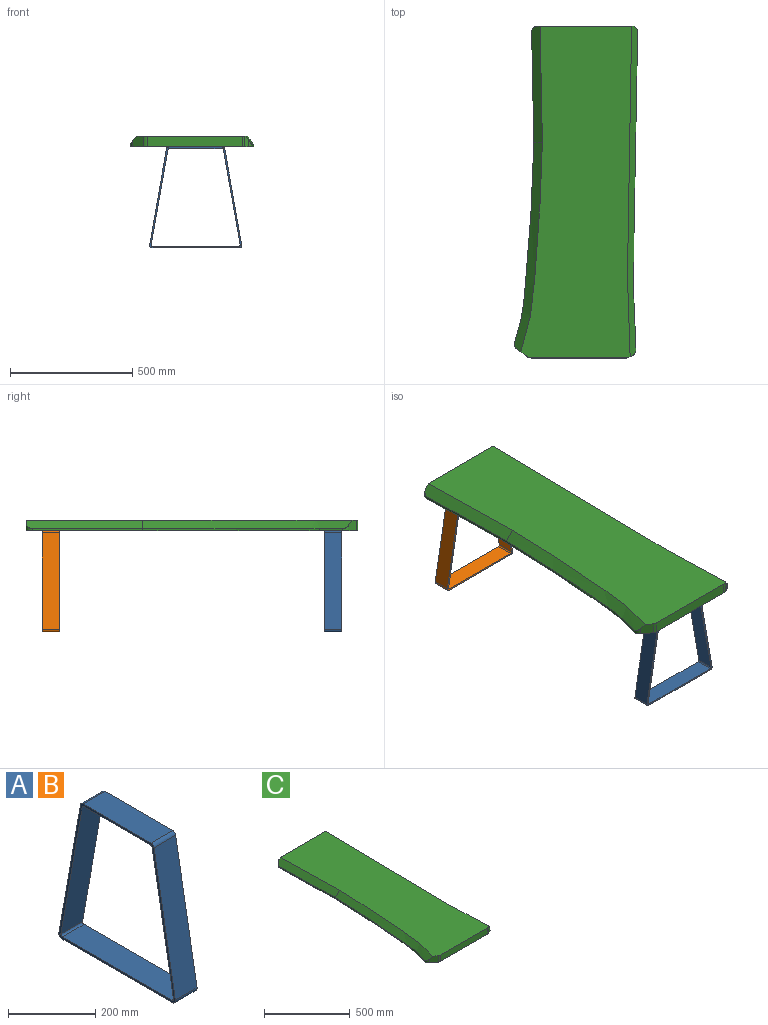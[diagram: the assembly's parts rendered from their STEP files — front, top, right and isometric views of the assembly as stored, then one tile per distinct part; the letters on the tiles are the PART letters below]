
ASSEMBLY  parts=3 mates=2
PART A: 18 faces, bbox 70x377.2x412.8 mm
  f0: plane 412.75x377.17mm, normal (1,0,0), area 9004.4mm2, adj f2,f3,f4,f5,f6,f7,f8,f9
  f1: plane 412.75x377.17mm, normal (-1,0,0), area 9004.4mm2, adj f2,f3,f4,f5,f6,f7,f8,f9
  f2: plane 353.95x70mm, normal (0,0,1), area 24776.3mm2, adj f0,f1,f10,f16
  f3: plane 390.05x70mm, normal (0,0.98,-0.17), area 27724.7mm2, adj f0,f1,f10,f11
  f4: plane 216.39x70mm, normal (0,0,-1), area 15147.6mm2, adj f0,f1,f11,f17
  f5: plane 357.17x70mm, normal (0,0,-1), area 25001.5mm2, adj f0,f1,f8,f14
  f6: plane 392.75x70mm, normal (0,-0.98,0.17), area 27916.6mm2, adj f0,f1,f8,f9
  f7: plane 218.66x70mm, normal (0,0,1), area 15306.2mm2, adj f0,f1,f9,f15
  f8: cylinder r=10mm len=70mm, axis (-1,0,0), area 1221.7mm2, adj f0,f1,f5,f6
  f9: cylinder r=10mm len=70mm, axis (-1,0,0), area 977.4mm2, adj f0,f1,f6,f7
  f10: cylinder r=5mm len=70mm, axis (1,0,0), area 610.9mm2, adj f0,f1,f2,f3
  f11: cylinder r=5mm len=70mm, axis (1,0,0), area 488.7mm2, adj f0,f1,f3,f4
  f12: plane 390.05x70mm, normal (0,-0.98,-0.17), area 27724.7mm2, adj f0,f1,f16,f17
  f13: plane 392.75x70mm, normal (0,0.98,0.17), area 27916.6mm2, adj f0,f1,f14,f15
  f14: cylinder r=10mm len=70mm, axis (-1,0,0), area 1221.7mm2, adj f0,f1,f5,f13
  f15: cylinder r=10mm len=70mm, axis (-1,0,0), area 977.4mm2, adj f0,f1,f7,f13
  f16: cylinder r=5mm len=70mm, axis (1,0,0), area 610.9mm2, adj f0,f1,f2,f12
  f17: cylinder r=5mm len=70mm, axis (1,0,0), area 488.7mm2, adj f0,f1,f4,f12
PART B: same geometry as A
PART C: 19 faces, bbox 544.3x1462x64.4 mm
  f0: plane 44.45x42.96mm, normal (-0.6,-0.8,0), area 2184.6mm2, adj f8,f9,f10,f15,f17
  f1: plane 388.94x44.45mm, normal (0,-1,0), area 17288.4mm2, adj f8,f9,f10,f11
  f2: plane 44.45x14.91mm, normal (0.42,-0.91,0), area 663.5mm2, adj f8,f9,f11,f12,f18
  f3: extruded ~1299x16.62mm, area 11366.3mm2, adj f9,f12,f13,f18
  f4: plane 383.29x44.45mm, normal (0,1,0), area 16992.2mm2, adj f8,f9,f13,f14,f16
  f5: plane 452.2x9.45mm, normal (-1,-0.02,0), area 4274.1mm2, adj f6,f9,f14,f16
  f6: extruded ~721.62x52.75mm, area 6842.8mm2, adj f5,f7,f9,f17
  f7: plane 94.74x25.93mm, normal (-0.96,0.26,0), area 927.8mm2, adj f6,f9,f15,f17
  f8: plane 1377.56x472.82mm, normal (0,0,1), area 506774.7mm2, adj f0,f1,f2,f4,f10,f11,f13,f16
  f9: plane 1357.59x504.38mm, normal (0,0,-1), area 587734mm2, adj f0,f1,f2,f3,f4,f5,f6,f7
  f10: cylinder r=25mm len=44.45mm, axis (0,0,-1), area 711.1mm2, adj f0,f1,f8,f9
  f11: cylinder r=25mm len=44.45mm, axis (0,0,1), area 486.2mm2, adj f1,f2,f8,f9
  f12: cylinder r=25mm len=31.03mm, axis (0,0,-1), area 585.1mm2, adj f2,f3,f9,f18
  f13: cylinder r=25mm len=44.45mm, axis (0,0,-1), area 876.6mm2, adj f3,f4,f8,f9,f18
  f14: cylinder r=25mm len=34.94mm, axis (0,0,-1), area 744.9mm2, adj f4,f5,f9,f16
  f15: cylinder r=25mm len=26.65mm, axis (0,0,-1), area 520.9mm2, adj f0,f7,f9,f17
  f16: plane 477.69x43.87mm, normal (-0.71,-0.01,0.71), area 23433.4mm2, adj f4,f5,f8,f14,f17
  f17: bspline ~897.45x133.19mm, area 41941.9mm2, adj f0,f6,f7,f8,f15,f16
  f18: bspline ~1433.55x43.57mm, area 58247.6mm2, adj f2,f3,f8,f12,f13
PLACE A rot(axis=(0,0,-1),90deg) t=(16.54,-605.19,0)mm
PLACE B rot(axis=(0,0,-1),90deg) t=(16.54,549.2,0)mm
PLACE C at identity fixed
MATE fastened C.f9 <-> B.f7  axis (0,0,-1) through (16.54,584.2,0)mm
MATE fastened C.f9 <-> A.f7  axis (0,0,-1) through (16.54,-570.19,0)mm
